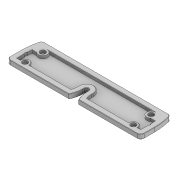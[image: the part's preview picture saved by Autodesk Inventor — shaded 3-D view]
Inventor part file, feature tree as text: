
AUTODESK INVENTOR PART (.ipt)
format: ipt  version: 2021 (Build 250183000, 183)  size: 670,720 bytes
history: native  units: mm
features: delete_face x8, projected_geometry x7, sketch x4, extrude x4, other x3, chamfer x2, reference x2
ambient origin geometry x8: Origin, YZ Plane, XZ Plane, XY Plane, X Axis, Y Axis, Z Axis, Center Point
bodies: Volumenkörper1 (feature_tree), Body1 (feature_tree)
feature tree (30):
  delete_face  "Fläche löschen1"
  sketch  "Skizze2"  dims[d0=4.8mm d1=16.0mm]
  delete_face  "Fläche löschen2"
  extrude  "Extrusion1"  Depth=16.0mm
  extrude  "Extrusion2"  Depth=10.0mm
  delete_face  "Fläche löschen3"
  chamfer  "Fase1"  Distance=10.0mm
  chamfer  "Fase2"  Distance=0.4mm Angle=45.0deg
  extrude  "Extrusion3"  Depth=0.25mm TaperAngle=0.0deg
  delete_face  "Fläche löschen4"
  delete_face  "Fläche löschen5"
  delete_face  "Fläche löschen6"
  delete_face  "Fläche löschen7"
  delete_face  "Fläche löschen8"
  extrude  "Extrusion4"  Depth=0.25mm
  reference  "Referenz1"
  projected_geometry  "Projizierte Kontur2"
  sketch  "Skizze3"  dims[d2=10.0mm d3=0.0mm d4=4.8mm d5=10.0mm d6=0.0mm d7=0.4mm d8=2.0mm d9=45.0deg]
  projected_geometry  "Projizierte Kontur3"
  reference  "Referenz2"
  sketch  "Skizze4"  dims[d10=0.4mm d11=2.0mm d12=45.0deg d13=0.25mm d14=0.0mm]
  projected_geometry  "Projizierte Kontur4"
  projected_geometry  "Projizierte Kontur5"
  projected_geometry  "Projizierte Kontur6"
  projected_geometry  "Projizierte Kontur7"
  sketch  "Skizze6"  dims[d19=6.15mm d20=6.15mm d21=6.15mm d22=6.15mm d23=0.25mm d24=0.0mm]
  projected_geometry  "Projizierte Kontur9"
  other  "Baugruppe2"
  other  "Grill:1"
  other  "Exhaust_Housing_Thread_Left:1"
